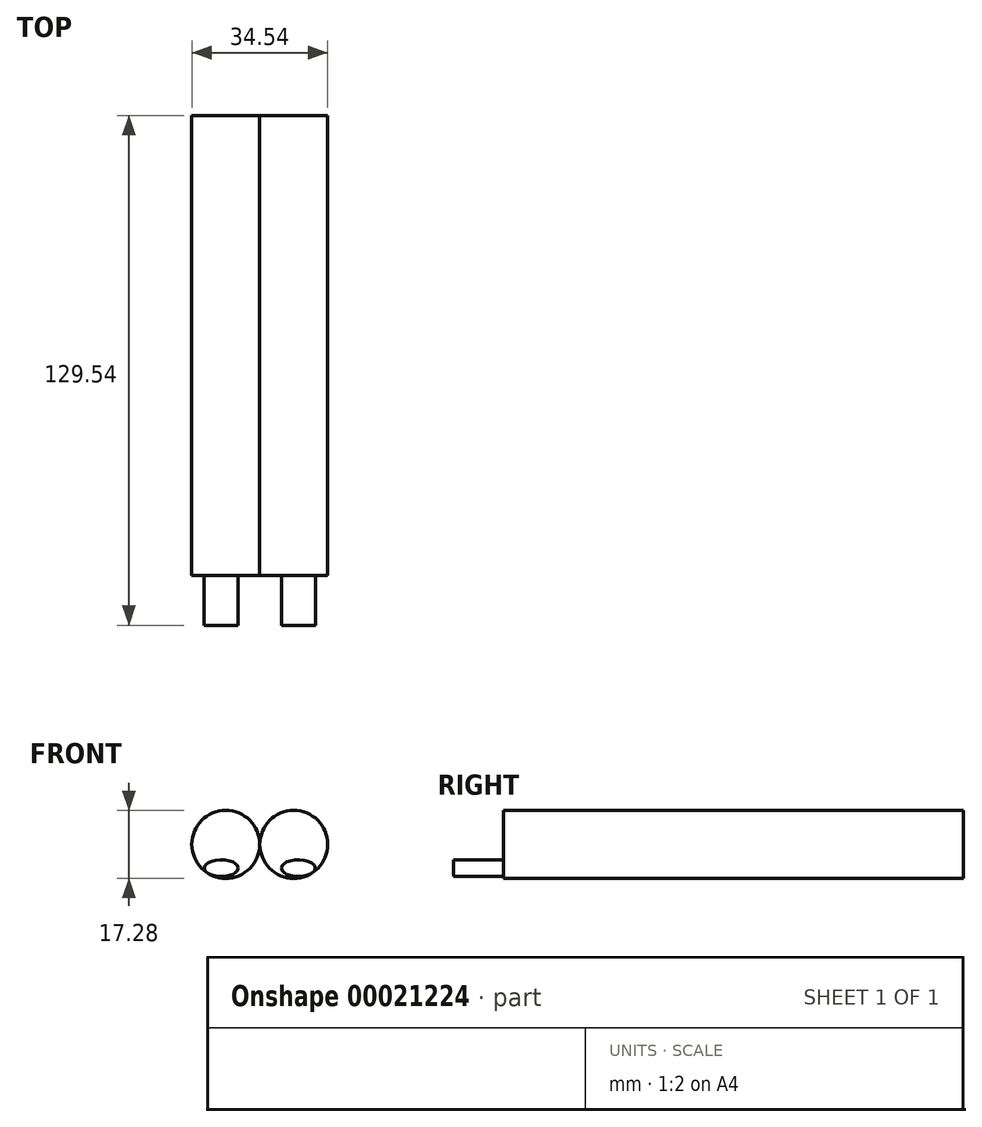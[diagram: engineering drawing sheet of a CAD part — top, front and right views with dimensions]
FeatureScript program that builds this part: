
annotation { "Feature Type Name" : "Feature", "Feature Type Description" : "" }
export const myFeature = defineFeature(function(context is Context, id is Id, definition is map)
    precondition{}
    {
        {
            var Q0;
            Q0=qCreatedBy(makeId("Front.planeOp"),FACE);
            var sketch = newSketch(context, id + "F0", { "sketchPlane" : qUnion([Q0])});
            skCircle(sketch, "E0", {"center": v(-8.64, 0) * mm, "radius": 8.64 * mm});
            skCircle(sketch, "E1.MirrorC", {"center": v(8.64, 0) * mm, "radius": 8.64 * mm});
            skLineSegment(sketch, "E2", {"start": v(0, 17) * mm, "end": v(0, -18.1) * mm, "construction": true});
            skSolve(sketch);
        }
        {
            var Q0;
            Q0 = qSketchRegion(id + "F0", true);
            extrude(context, id + "F1", {"entities" : qUnion([Q0]), "depth" : 58.42 * mm, "hasSecondDirection" : true, "secondDirectionOppositeDirection" : true, "secondDirectionDepth" : 58.42 * mm});
        }
        {
            var Q0;
            Q0=makeQuery(id+"F1.opExtrude","CAP_FACE",FACE,{"disambiguationData":[OSD([sQuery(id+"F0.wireOp",EDGE,"E0")])],"isStart":false});
            var sketch = newSketch(context, id + "F2", { "sketchPlane" : qUnion([Q0])});
            skEllipse(sketch, "E3", {"center": v(-9.8, -6.03) * mm, "majorRadius": 4.33 * mm, "minorRadius": 2.1 * mm, "majorAxis": v(1, 0)});
            skEllipse(sketch, "E4.MirrorC", {"center": v(9.8, -6.03) * mm, "majorRadius": 4.33 * mm, "minorRadius": 2.1 * mm, "majorAxis": v(-1, 0)});
            skSolve(sketch);
        }
        {
            var Q0;
            Q0 = qSketchRegion(id + "F2", true);
            extrude(context, id + "F3", {"entities" : qUnion([Q0]), "operationType" : NewBodyOperationType.ADD, "depth" : 12.7 * mm});
        }
    });
